# Revit family: Shower-Showerhead_Handshower_Set-KOHLER-STRAYT-K-45372T
name_source: partatom
category: Plumbing Fixtures
revit_build: Autodesk Revit 2017 (Build: 20160225_1515(x64)
units: mm (PartAtom-declared; Revit-internal decimal feet)

## family parameters
Cut with Voids When Loaded = No
Host = Face
OmniClass Number = 23.31.17.00
OmniClass Title = Showers
Part Type = Normal
Room Calculation Point = No
Round Connector Dimension = Use Diameter
Shared = No

## types (3) — shared parameters
ADA Compliant = No
Assembly Code = D2010700
CW Connection = Yes
Cold Water Inlet = Cold Water Inlet
Date Modified = 09/14/2020
Default Elevation = 39 3/8"
Description = Three-outlet shower column hard pipe connection
Drain Included = No
Finish = Kohler-Metal-CP-Polished_Chrome
Flow Rate = 0 GPM
HW Connection = Yes
Height = 42 5/8"
Hot Water Inlet = Hot Water Inlet
Length = 23 9/16"
Manufacturer = KOHLER Co.
Master Format 2014 = 22 42 23
Master Format 2014 Name = Residential Showers
Material = Premium Metal Construction
Panel Thickness = 0"
Pressure = 72.52 psi
Product Documentation Link = https://files.kohler.com.cn
Product Name = STRAYT
Product Page URL = https://www.kohler.com.cn
URL = http://www.kohler.com.cn
Vent Connection = No
Waste Connection = No
Waste Water Outlet = Waste Water Outlet
WaterSense Certified = No
Width = 11 1/4"

## per-type parameters (varying)
| type | Model | Type | With Carmine Handle Design | With Creamy White Handle Design | Without Design |
| CP- Polished Chrome | K-45372T-C4-CP | 1 | No | No | Yes |
| With Carmine Handle Design, CP- Polished Chrome | K-45372T-C4DPR-CP | 2 | Yes | No | No |
| With Creamy White Handle Design, CP-Polished Chrome | K-45372T-C4DPW-CP | 3 | No | Yes | No |

## geometry (parser evidence)
native form markers: Sweep x4
no freeform markers — native parametric forms only
